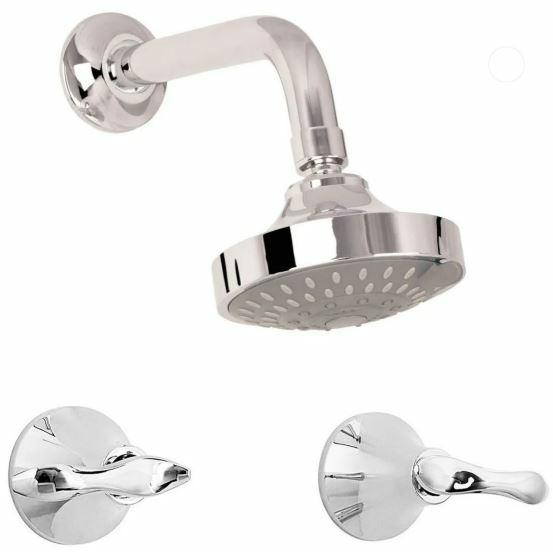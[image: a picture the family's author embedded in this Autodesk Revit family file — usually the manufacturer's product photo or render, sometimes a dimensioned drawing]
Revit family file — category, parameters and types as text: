
# Revit family: 01-1835-11 MEZCLADOR DUCHA 8” SIN SALIDA TINA TEDESCA
name_source: partatom
category: Plumbing Fixtures
revit_build: Autodesk Revit 2018 (Build: 20170223_1515(x64)
units: mm (PartAtom-declared; Revit-internal decimal feet)

## family parameters
Cut with Voids When Loaded = No
Host = Face
OmniClass Number = 23.31.11.00
Part Type = Normal
Room Calculation Point = No
Round Connector Dimension = Use Diameter
Shared = No

## types (1)
- 01-1835-11
    Ancho escudo = 60 mm  [stored 0.19685 ft]
    CW Connection = Yes
    Default Elevation = 0 mm  [stored 0 ft]
    Description = Mezclador ducha
    Distancia entre griferias = 203.2 mm  [stored 0.666667 ft]
    HW Connection = Yes
    Link Ficha Tecnica = No encontrada en internet
    Manija = 80 mm  [stored 0.262467 ft]
    Manufacturer = Gricol
    Model = 01-1835-11
    Plastico ABS Cromado = Plastico - ABS Cromado
    Plastico Acrilico Transparente = Plastico Acrilico Transparente
    Product Name = MEZCLADOR DUCHA 8” SIN SALIDA TINA TEDESCA
    Type Image = MEZCLADOR DUCHA 8” SIN SALIDA TINA TEDESCA.JPG
    URL = https://www.gricol.com
    Vent Connection = No
    Waste Connection = No

note: [stored X ft] marks values corroborated as IEEE doubles in the binary element streams (Revit-internal decimal feet)

## geometry (parser evidence)
native form markers: Blend x4, Sweep x28
no freeform markers — native parametric forms only
